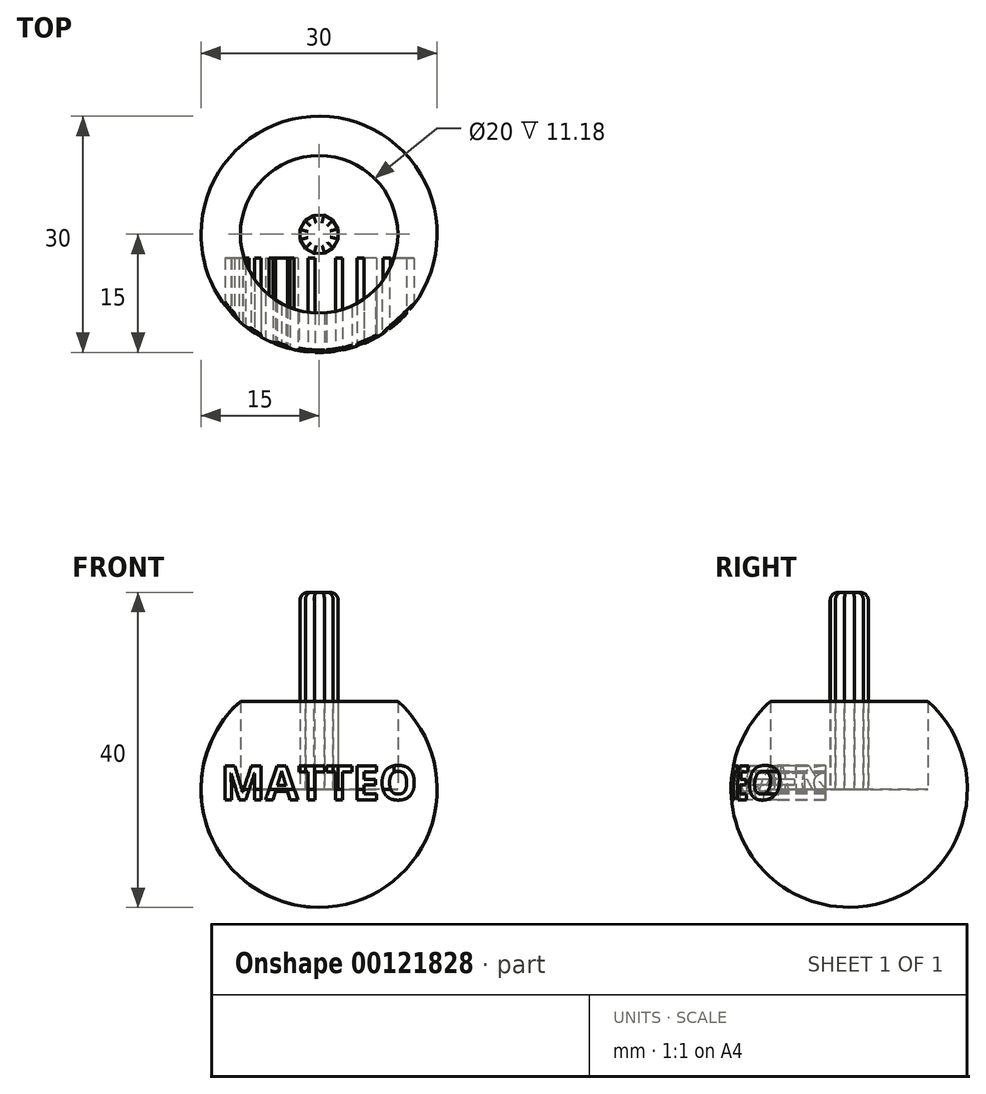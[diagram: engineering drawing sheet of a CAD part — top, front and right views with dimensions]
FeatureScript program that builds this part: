
annotation { "Feature Type Name" : "Feature", "Feature Type Description" : "" }
export const myFeature = defineFeature(function(context is Context, id is Id, definition is map)
    precondition{}
    {
        {
            var Q0;
            Q0=qCreatedBy(makeId("Front.planeOp"),FACE);
            var sketch = newSketch(context, id + "F0", { "sketchPlane" : qUnion([Q0])});
            skCircle(sketch, "E0", {"center": v(0, 0) * mm, "radius": 15 * mm});
            skLineSegment(sketch, "E1", {"start": v(0, 15) * mm, "end": v(0, -15) * mm});
            skSolve(sketch);
        }
        {
            var Q0;
            {var subQ0=sQuery(id+"F0.wireOp",EDGE,"E1");Q0=makeQuery(id+"F0.imprint","IMPRINT",FACE,{"disambiguationData":[TD([[makeQuery(id+"F0.imprint","IMPRINT",EDGE,{"derivedFrom":subQ0}),1.0]])]});}
            var Q1;
            Q1=sQuery(id+"F0.wireOp",EDGE,"E1");
            revolve(context, id + "F1", {"entities" : qUnion([Q0]), "axis" : qUnion([Q1]), "revolveType" : RevolveType.FULL});
        }
        {
            var Q0;
            Q0=qCreatedBy(makeId("Top.planeOp"),FACE);
            var sketch = newSketch(context, id + "F2", { "sketchPlane" : qUnion([Q0])});
            skCircle(sketch, "E2", {"center": v(0, 0) * mm, "radius": 10 * mm});
            skSolve(sketch);
        }
        {
            var Q0;
            Q0=qSketchRegion(id+"F2",true);
            extrude(context, id + "F3", {"entities" : qUnion([Q0]), "operationType" : NewBodyOperationType.REMOVE, "endBound" : BoundingType.THROUGH_ALL, "depth" : 25 * mm});
        }
        {
            var Q0;
            Q0=makeQuery(id+"F3.boolean.opBoolean","COPY",FACE,{"derivedFrom":makeQuery(id+"F3.opExtrude","CAP_FACE",FACE,{"disambiguationData":[OSD([sQuery(id+"F2.wireOp",EDGE,"E2")])],"isStart":true})});
            var sketch = newSketch(context, id + "F4", { "sketchPlane" : qUnion([Q0])});
            skLineSegment(sketch, "E3.0", {"start": v(1.74, 1.8) * mm, "end": v(2.4, 0.69) * mm});
            skLineSegment(sketch, "E3.1", {"start": v(2.4, 0.69) * mm, "end": v(2.43, -0.6) * mm});
            skLineSegment(sketch, "E3.2", {"start": v(2.43, -0.6) * mm, "end": v(1.8, -1.74) * mm});
            skLineSegment(sketch, "E3.3", {"start": v(1.8, -1.74) * mm, "end": v(0.69, -2.4) * mm});
            skLineSegment(sketch, "E3.4", {"start": v(0.69, -2.4) * mm, "end": v(-0.6, -2.43) * mm});
            skLineSegment(sketch, "E3.5", {"start": v(-0.6, -2.43) * mm, "end": v(-1.74, -1.8) * mm});
            skLineSegment(sketch, "E3.6", {"start": v(-1.74, -1.8) * mm, "end": v(-2.4, -0.69) * mm});
            skLineSegment(sketch, "E3.7", {"start": v(-2.4, -0.69) * mm, "end": v(-2.43, 0.6) * mm});
            skLineSegment(sketch, "E3.8", {"start": v(-2.43, 0.6) * mm, "end": v(-1.8, 1.74) * mm});
            skLineSegment(sketch, "E3.9", {"start": v(-1.8, 1.74) * mm, "end": v(-0.69, 2.4) * mm});
            skLineSegment(sketch, "E3.10", {"start": v(-0.69, 2.4) * mm, "end": v(0.6, 2.43) * mm});
            skLineSegment(sketch, "E3.11", {"start": v(0.6, 2.43) * mm, "end": v(1.74, 1.8) * mm});
            skSolve(sketch);
        }
        {
            var Q0;
            Q0=qSketchRegion(id+"F4",true);
            var Q1;
            Q1=sQuery(id+"F4.wireOp",EDGE,"S97E8AI5-NW8L-wBsM-i697-oy4Mv86zWIqM");
            extrude(context, id + "F5", {"entities" : qUnion([Q0]), "operationType" : NewBodyOperationType.ADD, "surfaceEntities" : qUnion([Q1]), "depth" : 25 * mm});
        }
        {
            var Q0;
            Q0=makeQuery(id+"F5.opExtrude","CAP_FACE",FACE,{"disambiguationData":[OSD([sQuery(id+"F4.wireOp",EDGE,"E3.0"),sQuery(id+"F4.wireOp",EDGE,"E3.1"),sQuery(id+"F4.wireOp",EDGE,"E3.2"),sQuery(id+"F4.wireOp",EDGE,"E3.3"),sQuery(id+"F4.wireOp",EDGE,"E3.4"),sQuery(id+"F4.wireOp",EDGE,"E3.5"),sQuery(id+"F4.wireOp",EDGE,"E3.6"),sQuery(id+"F4.wireOp",EDGE,"E3.7"),sQuery(id+"F4.wireOp",EDGE,"E3.8"),sQuery(id+"F4.wireOp",EDGE,"E3.9"),sQuery(id+"F4.wireOp",EDGE,"E3.10"),sQuery(id+"F4.wireOp",EDGE,"E3.11")])],"isStart":false});
            fillet(context, id + "F6", {"entities" : qUnion([Q0]), "radius" : 1 * mm, "tangentPropagation" : true, "allowEdgeOverflow" : false});
        }
        {
            var Q0;
            Q0=qCreatedBy(makeId("Front.planeOp"),FACE);
            cPlane(context, id + "F7", {"entities" : qUnion([Q0]), "cplaneType" : CPlaneType.OFFSET, "offset" : 25 * mm, "width" : 150 * mm, "height" : 150 * mm});
        }
        {
            var Q0;
            Q0=qCreatedBy(id+"F7.planeOp",FACE);
            var sketch = newSketch(context, id + "F8", { "sketchPlane" : qUnion([Q0])});
            skText(sketch, "E4", { "text": "MATTEO", "fontName": "OpenSans-Bold.ttf"});
            const initialGuessF8  = {"E4": [-0.0125, -0.00133, 1, 0, 0.00433]};
            skSetInitialGuess(sketch, initialGuessF8);
            skSolve(sketch);
        }
        {
            var Q0;
            Q0=qSketchRegion(id+"F8",true);
            extrude(context, id + "F9", {"entities" : qUnion([Q0]), "operationType" : NewBodyOperationType.REMOVE, "oppositeDirection" : true, "depth" : 22 * mm});
        }
    });
